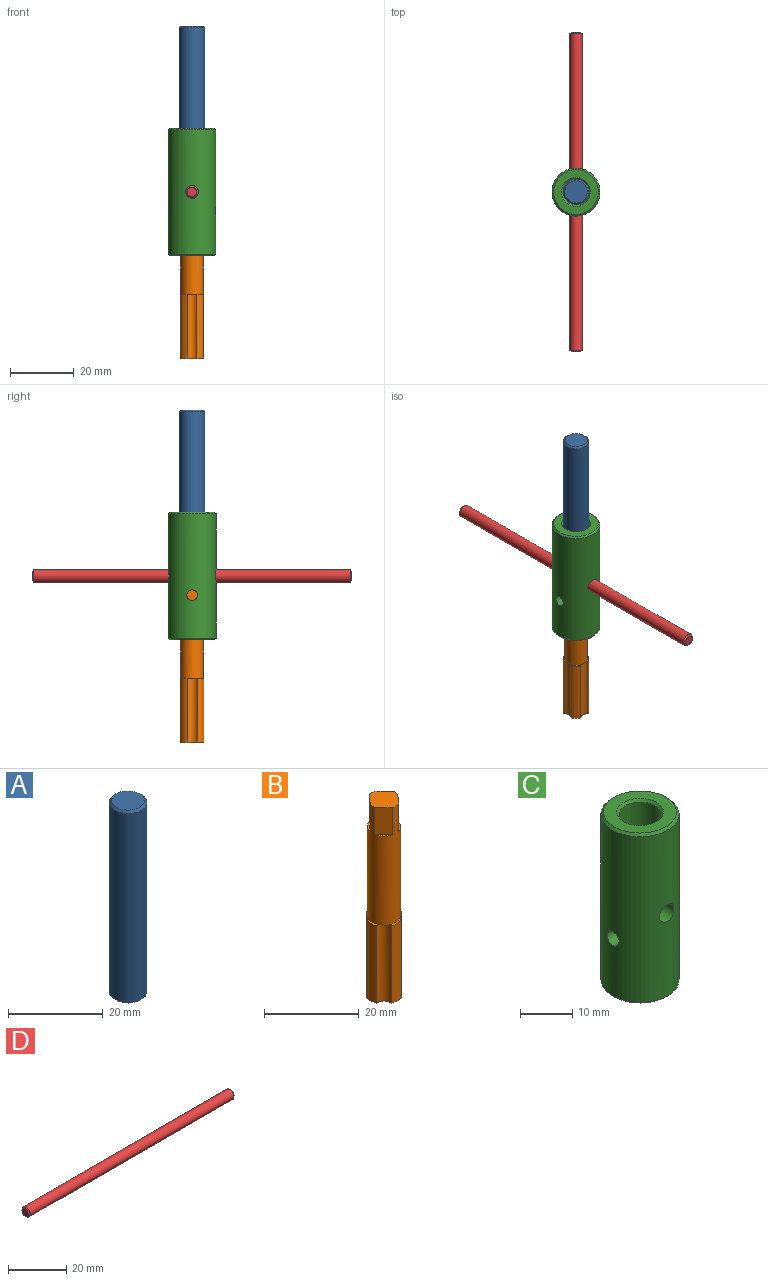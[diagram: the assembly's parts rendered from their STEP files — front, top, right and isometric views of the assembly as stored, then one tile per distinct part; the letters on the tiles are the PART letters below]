
ASSEMBLY  parts=4 mates=3
PART A: 5 faces, bbox 8x8x50 mm
  f0: cylinder r=4mm len=49mm, axis (0,0,-1), area 1231.5mm2, adj f3,f4
  f1: plane 7x7mm, normal (0,0,1), area 38.5mm2, adj f4
  f2: plane 7x7mm, normal (0,0,-1), area 38.5mm2, adj f3
  f3: cone r=4mm half-angle=45deg, axis (0,0,1), area 16.7mm2, adj f0,f2
  f4: cone r=3.5mm half-angle=45deg, axis (0,0,-1), area 16.7mm2, adj f0,f1
PART B: 27 faces, bbox 8x8x50 mm
  f0: plane 8x8mm, normal (0,0,-1), area 41.3mm2, adj f1,f2,f3,f8,f20,f22,f24,f26
  f1: cylinder r=4mm len=20mm, axis (0,0,-1), area 62mm2, adj f0,f4,f24,f26
  f2: cylinder r=4mm len=20mm, axis (0,0,-1), area 62mm2, adj f0,f5,f22,f24
  f3: cylinder r=4mm len=20mm, axis (0,0,-1), area 62mm2, adj f0,f6,f20,f22
  f4: plane 3.06x0.85mm, normal (0,0,1), area 1.6mm2, adj f1,f10,f24,f26
  f5: plane 3.06x0.85mm, normal (0,0,1), area 1.6mm2, adj f2,f10,f22,f24
  f6: plane 3.06x0.85mm, normal (0,0,1), area 1.6mm2, adj f3,f10,f20,f22
  f7: plane 7x7mm, normal (0,0,1), area 33.5mm2, adj f10,f11,f13,f15,f17
  f8: cylinder r=4mm len=20mm, axis (0,0,-1), area 62mm2, adj f0,f9,f20,f26
  f9: plane 3.06x0.85mm, normal (0,0,1), area 1.6mm2, adj f8,f10,f20,f26
  f10: cylinder r=3.5mm len=30mm, axis (0,0,-1), area 552.7mm2, adj f4,f5,f6,f7,f9,f11,f12,f13
  f11: plane 7x2.67mm, normal (-0.73,0.68,0), area 25.4mm2, adj f7,f10,f12
  f12: plane 2.67x2.47mm, normal (0,0,1), area 1.3mm2, adj f10,f11
  f13: plane 7x2.67mm, normal (0.73,0.68,0), area 25.4mm2, adj f7,f10,f14
  f14: plane 2.67x2.47mm, normal (0,0,1), area 1.3mm2, adj f10,f13
  f15: plane 7x2.67mm, normal (0.73,-0.68,0), area 25.4mm2, adj f7,f10,f16
  f16: plane 2.67x2.47mm, normal (0,0,1), area 1.3mm2, adj f10,f15
  f17: plane 7x2.67mm, normal (-0.73,-0.68,0), area 25.4mm2, adj f7,f10,f18
  f18: plane 2.67x2.47mm, normal (0,0,1), area 1.3mm2, adj f10,f17
  f19: plane 1.62x1.62mm, normal (0,0,-1), area 0.9mm2, adj f10,f20
  f20: cylinder r=2mm len=20mm, axis (0,0,-1), area 71mm2, adj f0,f3,f6,f8,f9,f19
  f21: plane 1.62x1.62mm, normal (0,0,-1), area 0.9mm2, adj f10,f22
  f22: cylinder r=2mm len=20mm, axis (0,0,-1), area 71mm2, adj f0,f2,f3,f5,f6,f21
  f23: plane 1.62x1.62mm, normal (0,0,-1), area 0.9mm2, adj f10,f24
  f24: cylinder r=2mm len=20mm, axis (0,0,-1), area 71mm2, adj f0,f1,f2,f4,f5,f23
  f25: plane 1.62x1.62mm, normal (0,0,-1), area 0.9mm2, adj f10,f26
  f26: cylinder r=2mm len=20mm, axis (0,0,-1), area 71mm2, adj f0,f1,f4,f8,f9,f25
PART C: 15 faces, bbox 15x15x40 mm
  f0: cylinder r=3.5mm len=19.2mm, axis (0,0,-1), area 394mm2, adj f2,f3,f7,f11,f12,f13,f14
  f1: cylinder r=7.5mm len=39mm, axis (0,0,-1), area 1795.3mm2, adj f8,f10,f11,f12,f13,f14
  f2: cone r=0mm half-angle=59deg, axis (0,0,1), area 4.4mm2, adj f0,f4,f11,f12
  f3: cone r=0mm half-angle=59deg, axis (0,0,1), area 4.4mm2, adj f0,f4,f11,f12
  f4: cylinder r=4mm len=19.5mm, axis (0,0,1), area 477.1mm2, adj f2,f3,f9,f11,f12
  f5: plane 14x14mm, normal (0,0,1), area 90.3mm2, adj f9,f10
  f6: plane 14x14mm, normal (0,0,-1), area 103.7mm2, adj f7,f8
  f7: cone r=3.5mm half-angle=45deg, axis (0,0,-1), area 16.7mm2, adj f0,f6
  f8: cone r=7.5mm half-angle=45deg, axis (0,0,1), area 32.2mm2, adj f1,f6
  f9: cone r=4mm half-angle=45deg, axis (0,0,1), area 18.9mm2, adj f4,f5
  f10: cone r=7mm half-angle=45deg, axis (0,0,-1), area 32.2mm2, adj f1,f5
  f11: cylinder r=2mm len=4.61mm, axis (0,-1,0), area 48.8mm2, adj f0,f1,f2,f3,f4
  f12: cylinder r=2mm len=4.61mm, axis (0,-1,0), area 48.8mm2, adj f0,f1,f2,f3,f4
  f13: cylinder r=1.65mm len=4.41mm, axis (1,0,0), area 42.6mm2, adj f0,f1
  f14: cylinder r=1.65mm len=4.41mm, axis (1,0,0), area 42.6mm2, adj f0,f1
PART D: 5 faces, bbox 100x4x4 mm
  f0: cylinder r=2mm len=99mm, axis (-1,0,0), area 1244.1mm2, adj f3,f4
  f1: plane 3x3mm, normal (1,0,0), area 7.1mm2, adj f4
  f2: plane 3x3mm, normal (-1,0,0), area 7.1mm2, adj f3
  f3: cone r=2mm half-angle=45deg, axis (1,0,0), area 7.8mm2, adj f0,f2
  f4: cone r=1.5mm half-angle=45deg, axis (-1,0,0), area 7.8mm2, adj f0,f1
PLACE A at identity
PLACE B rot(axis=(0,0,1),45deg) t=(0,0,-54)mm
PLACE C t=(0,0,-22)mm
PLACE D rot(axis=(-0.58,-0.58,0.58),120deg) t=(0,-49.97,-2)mm
MATE cylindrical C.f1 <-> A.f0  axis (0,0,1) through (0,0,18)mm
MATE revolute C.f1 <-> B.f1  axis (0,0,-1) through (0,0,-22)mm
MATE fastened D.f0 <-> C.f11  axis (0,-1,0) through (0,0.03,-2)mm
